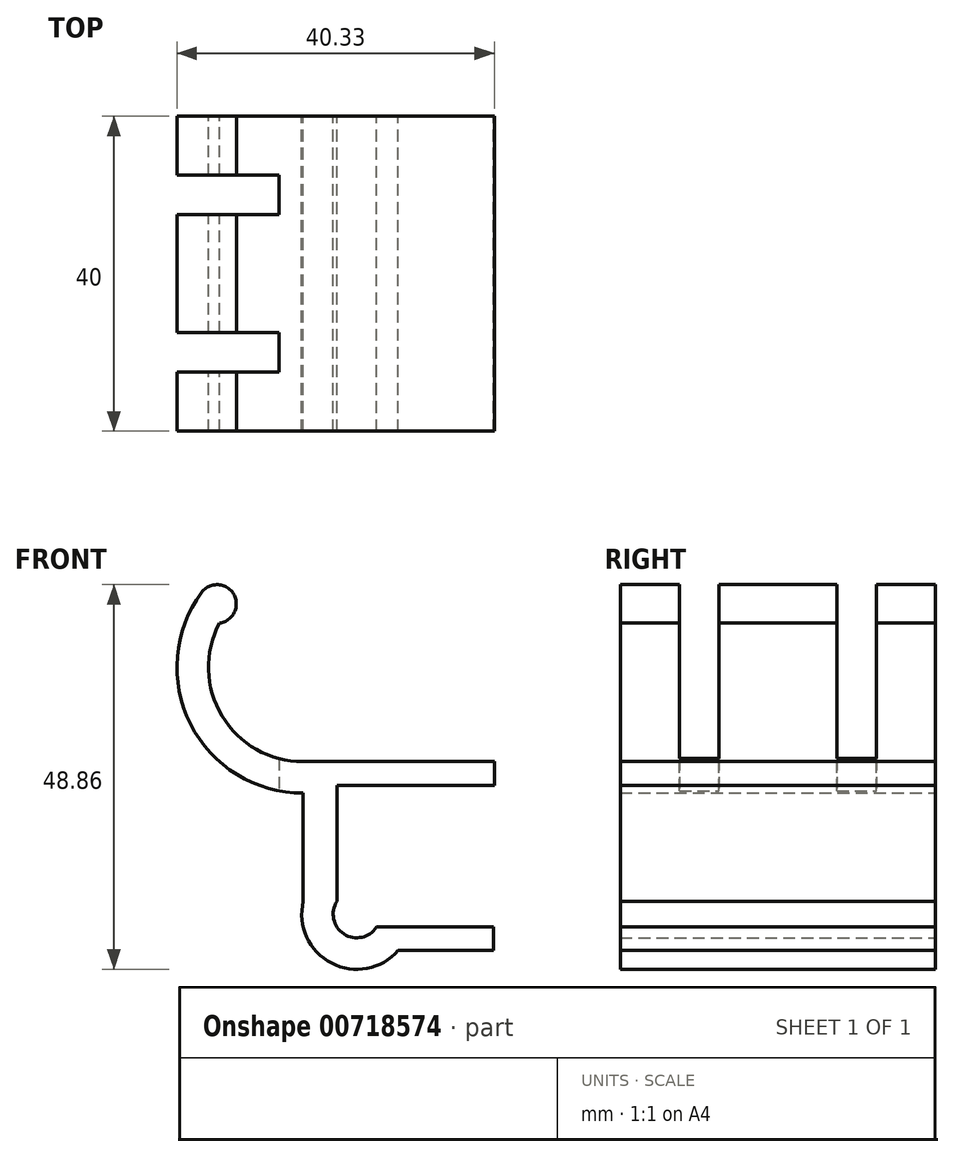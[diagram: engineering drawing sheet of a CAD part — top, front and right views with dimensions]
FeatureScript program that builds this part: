
annotation { "Feature Type Name" : "Feature", "Feature Type Description" : "" }
export const myFeature = defineFeature(function(context is Context, id is Id, definition is map)
    precondition{}
    {
        {
            var Q0;
            Q0=qCreatedBy(makeId("Front.planeOp"),FACE);
            var sketch = newSketch(context, id + "F0", { "sketchPlane" : qUnion([Q0])});
            skLineSegment(sketch, "E0.bottom", {"start": v(-7.72, 21) * mm, "end": v(-27.72, 21) * mm});
            skLineSegment(sketch, "E0.top", {"start": v(-7.72, 18) * mm, "end": v(-27.72, 18) * mm});
            skLineSegment(sketch, "E0.left", {"start": v(-7.72, 21) * mm, "end": v(-7.72, 18) * mm});
            skLineSegment(sketch, "E0.right", {"start": v(-27.72, 21) * mm, "end": v(-27.72, 18) * mm});
            skLineSegment(sketch, "E1.bottom", {"start": v(-27.72, 21) * mm, "end": v(-32.05, 21) * mm});
            skLineSegment(sketch, "E1.top", {"start": v(-27.72, 3.25) * mm, "end": v(-32.05, 3.25) * mm});
            skLineSegment(sketch, "E1.left", {"start": v(-27.72, 21) * mm, "end": v(-27.72, 3.25) * mm});
            skLineSegment(sketch, "E1.right", {"start": v(-32.05, 21) * mm, "end": v(-32.05, 3.25) * mm});
            skArc(sketch, "E2", {"start": v(-42.66, 38.6) * mm, "mid": v(-42.33, 26.8) * mm, "end": v(-32.05, 21) * mm});
            skArc(sketch, "E3.0", {"start": v(-44.93, 42.5) * mm, "mid": v(-46.33, 25.78) * mm, "end": v(-32.05, 17) * mm});
            skLineSegment(sketch, "E4", {"start": v(-42.66, 38.6) * mm, "end": v(-32.05, 21) * mm, "construction": true});
            skArc(sketch, "E5", {"start": v(-44.93, 42.5) * mm, "mid": v(-40.84, 42.28) * mm, "end": v(-42.66, 38.6) * mm});
            skArc(sketch, "E6", {"start": v(-27.72, 3.25) * mm, "mid": v(-26.83, -0.9) * mm, "end": v(-22.68, 0) * mm});
            skArc(sketch, "E7.0", {"start": v(-32, 3.25) * mm, "mid": v(-28.42, -4.59) * mm, "end": v(-19.95, -3) * mm});
            skLineSegment(sketch, "E8.bottom", {"start": v(-22.68, 0) * mm, "end": v(-7.81, 0) * mm});
            skLineSegment(sketch, "E8.top", {"start": v(-22.68, -3) * mm, "end": v(-7.81, -3) * mm});
            skLineSegment(sketch, "E8.left", {"start": v(-22.68, 0) * mm, "end": v(-22.68, -3) * mm});
            skLineSegment(sketch, "E8.right", {"start": v(-7.81, 0) * mm, "end": v(-7.81, -3) * mm});
            skLineSegment(sketch, "E9", {"start": v(-11.2, 18) * mm, "end": v(-11.2, 0) * mm, "construction": true});
            skSolve(sketch);
        }
        {
            var Q0;
            Q0 = qSketchRegion(id + "F0", true);
            extrude(context, id + "F1", {"entities" : qUnion([Q0]), "depth" : 40 * mm, "offsetDistance" : 25 * mm});
        }
        {
            var Q0;
            Q0=qCreatedBy(makeId("Top.planeOp"),FACE);
            var sketch = newSketch(context, id + "F2", { "sketchPlane" : qUnion([Q0])});
            skLineSegment(sketch, "E10.bottom", {"start": v(-56.34, -7.5) * mm, "end": v(-35.1, -7.5) * mm});
            skLineSegment(sketch, "E10.top", {"start": v(-56.34, -12.5) * mm, "end": v(-35.1, -12.5) * mm});
            skLineSegment(sketch, "E10.left", {"start": v(-56.34, -7.5) * mm, "end": v(-56.34, -12.5) * mm});
            skLineSegment(sketch, "E10.right", {"start": v(-35.1, -7.5) * mm, "end": v(-35.1, -12.5) * mm});
            skLineSegment(sketch, "E11.bottom", {"start": v(-56.34, -27.5) * mm, "end": v(-35.1, -27.5) * mm});
            skLineSegment(sketch, "E11.top", {"start": v(-56.34, -32.5) * mm, "end": v(-35.1, -32.5) * mm});
            skLineSegment(sketch, "E11.left", {"start": v(-56.34, -27.5) * mm, "end": v(-56.34, -32.5) * mm});
            skLineSegment(sketch, "E11.right", {"start": v(-35.1, -27.5) * mm, "end": v(-35.1, -32.5) * mm});
            skLineSegment(sketch, "E12", {"start": v(-49.7, -12.5) * mm, "end": v(-49.7, -27.5) * mm, "construction": true});
            skLineSegment(sketch, "E13", {"start": v(-49.7, -20) * mm, "end": v(-44.93, -20) * mm, "construction": true});
            skSolve(sketch);
        }
        {
            var Q0;
            Q0 = qSketchRegion(id + "F2", true);
            extrude(context, id + "F3", {"entities" : qUnion([Q0]), "operationType" : NewBodyOperationType.REMOVE, "oppositeDirection" : true, "depth" : -50 * mm, "offsetDistance" : 25 * mm});
        }
    });
